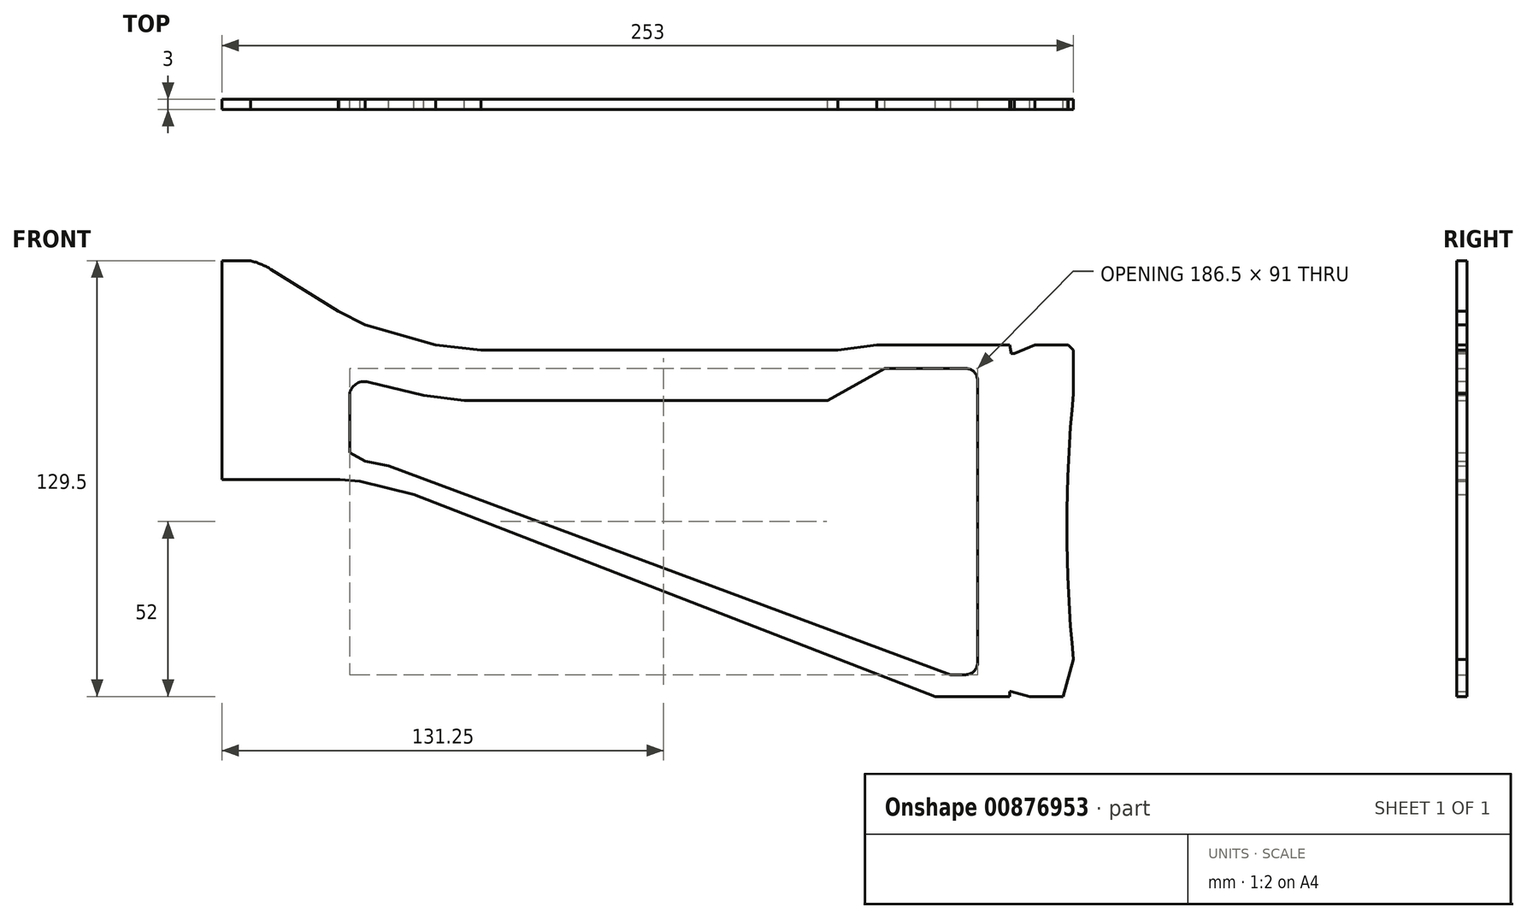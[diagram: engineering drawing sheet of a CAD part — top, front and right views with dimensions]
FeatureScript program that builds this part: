
annotation { "Feature Type Name" : "Feature", "Feature Type Description" : "" }
export const myFeature = defineFeature(function(context is Context, id is Id, definition is map)
    precondition{}
    {
        {
            var Q0;
            Q0=qCreatedBy(makeId("Front.planeOp"),FACE);
            var sketch = newSketch(context, id + "F0", { "sketchPlane" : qUnion([Q0])});
            skLineSegment(sketch, "E0", {"start": v(0, 0) * mm, "end": v(8.5, 0) * mm});
            skLineSegment(sketch, "E1", {"start": v(14.5, -2.5) * mm, "end": v(34.5, -15) * mm});
            skLineSegment(sketch, "E2", {"start": v(34.5, -15) * mm, "end": v(42.5, -19) * mm});
            skLineSegment(sketch, "E3", {"start": v(42.5, -19) * mm, "end": v(63.5, -25) * mm});
            skLineSegment(sketch, "E4", {"start": v(63.5, -25) * mm, "end": v(77, -26.5) * mm});
            skLineSegment(sketch, "E5", {"start": v(77, -26.5) * mm, "end": v(183, -26.5) * mm});
            skLineSegment(sketch, "E6", {"start": v(183, -26.5) * mm, "end": v(194.5, -25) * mm});
            skLineSegment(sketch, "E7", {"start": v(194.5, -25) * mm, "end": v(234, -25) * mm});
            skLineSegment(sketch, "E8", {"start": v(234, -25) * mm, "end": v(234.5, -27) * mm});
            skLineSegment(sketch, "E9", {"start": v(234.5, -27) * mm, "end": v(234.5, -27.5) * mm});
            skLineSegment(sketch, "E10", {"start": v(234.5, -27.5) * mm, "end": v(235.5, -27.5) * mm});
            skLineSegment(sketch, "E11", {"start": v(235.5, -27.5) * mm, "end": v(241.5, -25) * mm});
            skLineSegment(sketch, "E12", {"start": v(241.5, -25) * mm, "end": v(251.5, -25) * mm});
            skLineSegment(sketch, "E13", {"start": v(251.5, -25) * mm, "end": v(253, -26.5) * mm});
            skLineSegment(sketch, "E14", {"start": v(253, -26.5) * mm, "end": v(253, -39.5) * mm});
            skLineSegment(sketch, "E15", {"start": v(253, -118.5) * mm, "end": v(250, -129.5) * mm});
            skLineSegment(sketch, "E16", {"start": v(250, -129.5) * mm, "end": v(240, -129.5) * mm});
            skLineSegment(sketch, "E17", {"start": v(240, -129.5) * mm, "end": v(234.5, -128) * mm});
            skLineSegment(sketch, "E18", {"start": v(234.5, -128) * mm, "end": v(234, -128) * mm});
            skLineSegment(sketch, "E19", {"start": v(234, -128) * mm, "end": v(234, -129.5) * mm});
            skLineSegment(sketch, "E20", {"start": v(234, -129.5) * mm, "end": v(212, -129.5) * mm});
            skLineSegment(sketch, "E21", {"start": v(212, -129.5) * mm, "end": v(57, -69.5) * mm});
            skLineSegment(sketch, "E22", {"start": v(57, -69.5) * mm, "end": v(41, -65.5) * mm});
            skLineSegment(sketch, "E23", {"start": v(41, -65.5) * mm, "end": v(35, -65) * mm});
            skLineSegment(sketch, "E24", {"start": v(35, -65) * mm, "end": v(0, -65) * mm});
            skLineSegment(sketch, "E25", {"start": v(0, -65) * mm, "end": v(0, 0) * mm});
            skLineSegment(sketch, "E26", {"start": v(87, -41.5) * mm, "end": v(113, -41.5) * mm});
            skLineSegment(sketch, "E27", {"start": v(138, -41.5) * mm, "end": v(180, -41.5) * mm});
            skLineSegment(sketch, "E28", {"start": v(180, -41.5) * mm, "end": v(197, -32) * mm});
            skLineSegment(sketch, "E29", {"start": v(224.5, -35.5) * mm, "end": v(224.5, -119.5) * mm});
            skPoint(sketch, "E30", {"position": v(77, -41.5) * mm});
            skArc(sketch, "E31", {"start": v(14.5, -2.5) * mm, "mid": v(11.6, -1) * mm, "end": v(8.5, 0) * mm});
            skArc(sketch, "E32", {"start": v(253, -39.5) * mm, "mid": v(251.05, -79) * mm, "end": v(253, -118.5) * mm});
            skPoint(sketch, "E33", {"position": v(253, -79) * mm});
            skLineSegment(sketch, "E34", {"start": v(221, -32) * mm, "end": v(197, -32) * mm});
            skLineSegment(sketch, "E35", {"start": v(113, -41.5) * mm, "end": v(138, -41.5) * mm});
            skLineSegment(sketch, "E36", {"start": v(77, -41.5) * mm, "end": v(87, -41.5) * mm});
            skLineSegment(sketch, "E37", {"start": v(49.5, -61) * mm, "end": v(42.5, -59.5) * mm});
            skLineSegment(sketch, "E38", {"start": v(38, -57) * mm, "end": v(38, -39) * mm});
            skLineSegment(sketch, "E39", {"start": v(43.5, -36) * mm, "end": v(60, -40) * mm});
            skLineSegment(sketch, "E40", {"start": v(60, -40) * mm, "end": v(72, -41.5) * mm});
            skLineSegment(sketch, "E41", {"start": v(72, -41.5) * mm, "end": v(77, -41.5) * mm});
            skArc(sketch, "E42", {"start": v(224.5, -35.5) * mm, "mid": v(223.47, -33.03) * mm, "end": v(221, -32) * mm});
            skArc(sketch, "E43", {"start": v(43.5, -36) * mm, "mid": v(40.17, -36.44) * mm, "end": v(38, -39) * mm});
            skLineSegment(sketch, "E44", {"start": v(38, -57) * mm, "end": v(42.5, -59.5) * mm});
            skLineSegment(sketch, "E45", {"start": v(49.5, -61) * mm, "end": v(216.5, -123) * mm});
            skLineSegment(sketch, "E46", {"start": v(216.5, -123) * mm, "end": v(221, -123) * mm});
            skArc(sketch, "E47", {"start": v(224.5, -119.5) * mm, "mid": v(223.47, -121.97) * mm, "end": v(221, -123) * mm});
            skSolve(sketch);
        }
        {
            var Q0;
            Q0=makeQuery(id+"F0.imprint","IMPRINT",FACE,{"disambiguationData":[TD([[makeQuery(id+"F0.imprint","IMPRINT",EDGE,{"derivedFrom":sQuery(id+"F0.wireOp",EDGE,"E0")}),-1.0]])]});
            extrude(context, id + "F1", {"entities" : qUnion([Q0]), "depth" : 3 * mm, "offsetDistance" : 25 * mm});
        }
    });
